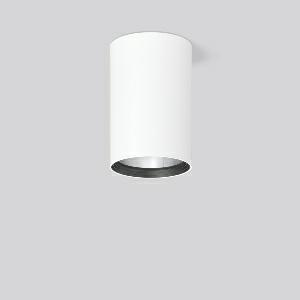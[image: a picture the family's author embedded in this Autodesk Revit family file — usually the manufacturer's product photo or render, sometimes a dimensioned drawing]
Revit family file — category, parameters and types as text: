
# Revit family: heledon_maxi_a_931230_002_76_3464
name_source: partatom
category: Lighting Fixtures
units: mm (PartAtom-declared; Revit-internal decimal feet)

## family parameters
Cut with Voids When Loaded = No
Host = Face
Light Source = No
Part Type = Normal
Room Calculation Point = No
Round Connector Dimension = Use Diameter
Shared = No

## types (1)
- HELEDON maxi A (1 x LED Modul 932 fresh meat, 2100 lm, 3200)
    Apparent Load = 33 VA
    Approval mark = CE
    CIE Flux Codes = 100 100 100 100 100
    Color Rendering = 90
    Color Temperature = 3200
    Default Elevation = 1800 mm
    Description = Series: HELEDON maxi
Cylindrical surface-mounted downlight. Housing: die-cast aluminium, powder-coated. Internal ceiling frame polycarbonate with bayonet mounting. Black plastic ring and recessed LED to prevent glare from the side. Optical assembly with reflector made of MIRO-Silver with 98% total light reflection for outstanding efficiency - can be changed without tools. Special LED for illumination of meat included. Suitable for Ceiling mounting. Easy installation with a separate ceiling frame with bayonet mounting and plug connection. Driver integrated. Connected via plug-in connector. High quality converter without flickering and stroboscopic effect. The following accessories can be mounted without use of tools: interchangeable lenses, decorative glasses, honeycomb louvre, clear and frosted diffusers, white interchangeable plastic ring. 
Colour: traffic white, matt (RAL 9016)
Diameter: 123 mm
Height: 183 mm
Lamp: LED
Socket: without socket
Colour temperature: fresh meat
System power: 33 W
Rated luminous flux: 2100 lm
Luminous efficiency: 64 lm/W
Control gear: Converter, dimmable, DALI
Protection class: I
Type of protection: IP 20
    Height = 183 mm
    Lamp = 1 x LED Modul 932 fresh meat
    Lamp Light Flux = 2100 lm
    Lamp count = 1
    Length = 123 mm
    Lifetime = 50000 h
    Luminous efficacy = 64 lm/W
    Manufacturer = RZB
    ModVariant = No
    Model = 931230.002.76
    Mounting Place = Ceiling
    Mounting Type = Surface mounted
    Number of Poles = 1
    OnlyDefault = Yes
    Power Factor = 1
    Product Name = HELEDON maxi A
    Product group = Surface mounted downlights
    ProductGroupID = 302
    Protection Class = Protection class I
    Protection Degree = IP 20
    RLX_Detail_Level = 1
    RLX_Emergency_Light_Flux = 0 lm
    RLX_Emergency_Type = 0
    RLX_Emergency_Type_DB = No
    RlxData = <blob elided: 98337 chars, md5=bd295953>
    Socket = socket
    Standby Power = 0 W
    System Light Flux = 2100 lm
    System Power = 33 W
    Type Comments = Product without accessories
    Type Image = 931192.002.jpg
    URL = http://relux.com
    VarID = ---
    Voltage = 230 V
    Voltage Range = 220-240 V
    Weight = 0.00 kg
    Width = 0 mm  [stored 0 ft]

note: [stored X ft] marks values corroborated as IEEE doubles in the binary element streams (Revit-internal decimal feet)

## geometry (parser evidence)
native form markers: Blend x4, Sweep x10
no freeform markers — native parametric forms only
